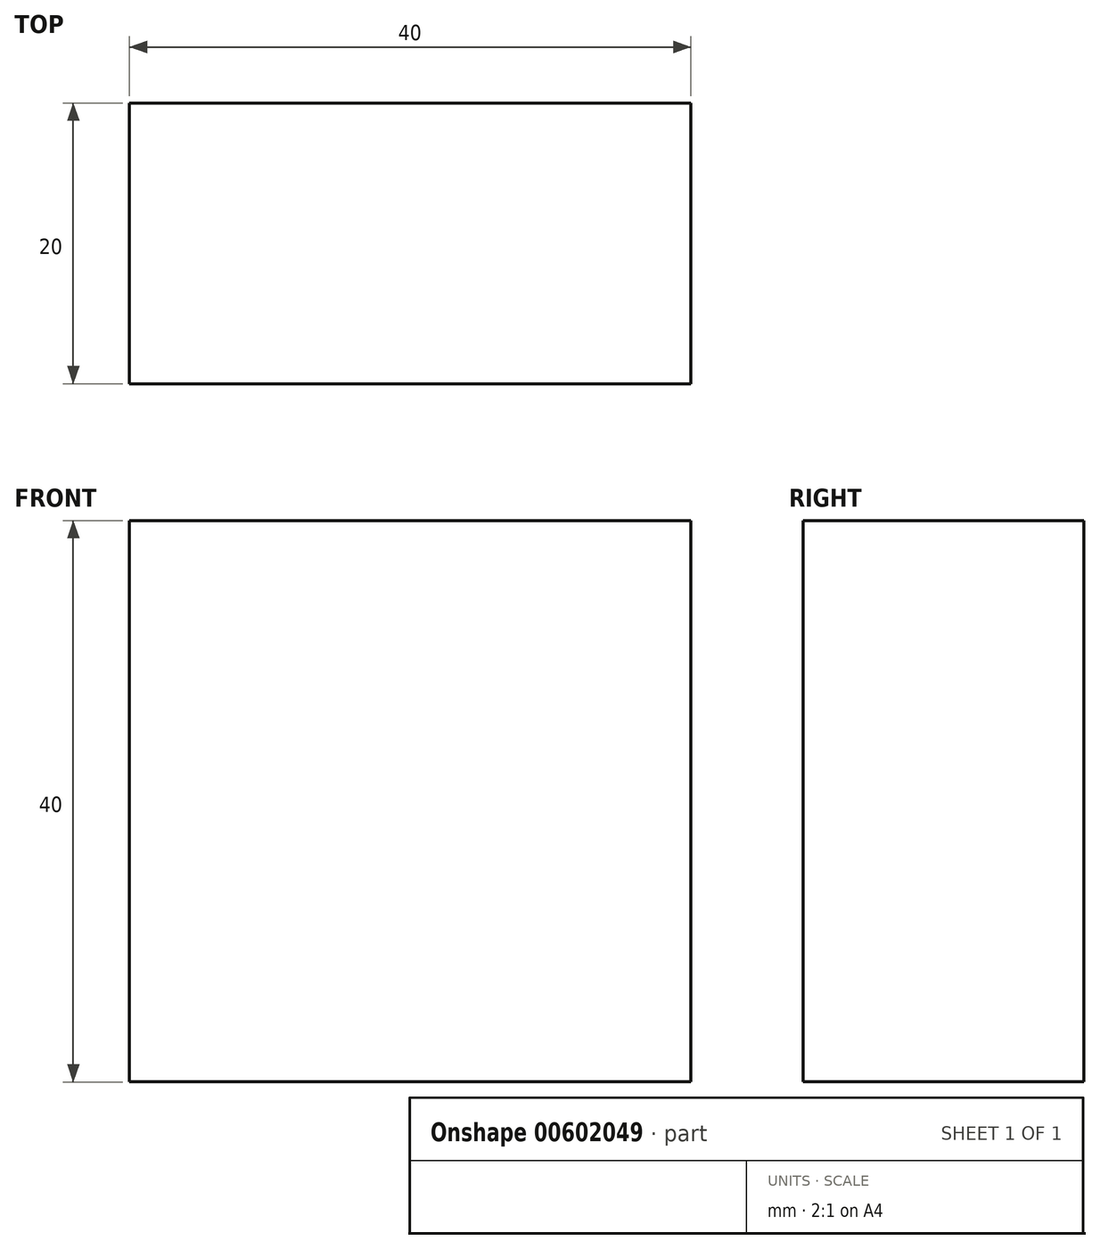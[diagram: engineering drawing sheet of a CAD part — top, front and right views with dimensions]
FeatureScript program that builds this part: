
annotation { "Feature Type Name" : "Feature", "Feature Type Description" : "" }
export const myFeature = defineFeature(function(context is Context, id is Id, definition is map)
    precondition{}
    {
        {
            var Q0;
            Q0=qCreatedBy(makeId("Front.planeOp"),FACE);
            var sketch = newSketch(context, id + "F0", { "sketchPlane" : qUnion([Q0])});
            skLineSegment(sketch, "E0", {"start": v(-61.4, 28.24) * mm, "end": v(-21.4, 28.24) * mm});
            skLineSegment(sketch, "E1", {"start": v(-21.4, 28.24) * mm, "end": v(-21.4, -11.76) * mm});
            skLineSegment(sketch, "E2", {"start": v(-21.4, -11.76) * mm, "end": v(-61.4, -11.76) * mm});
            skLineSegment(sketch, "E3", {"start": v(-61.4, -11.76) * mm, "end": v(-61.4, 28.24) * mm});
            skSolve(sketch);
        }
        {
            var Q0;
            Q0 = qSketchRegion(id + "F0", true);
            extrude(context, id + "F1", {"entities" : qUnion([Q0]), "depth" : 20 * mm, "offsetDistance" : 25 * mm});
        }
    });
